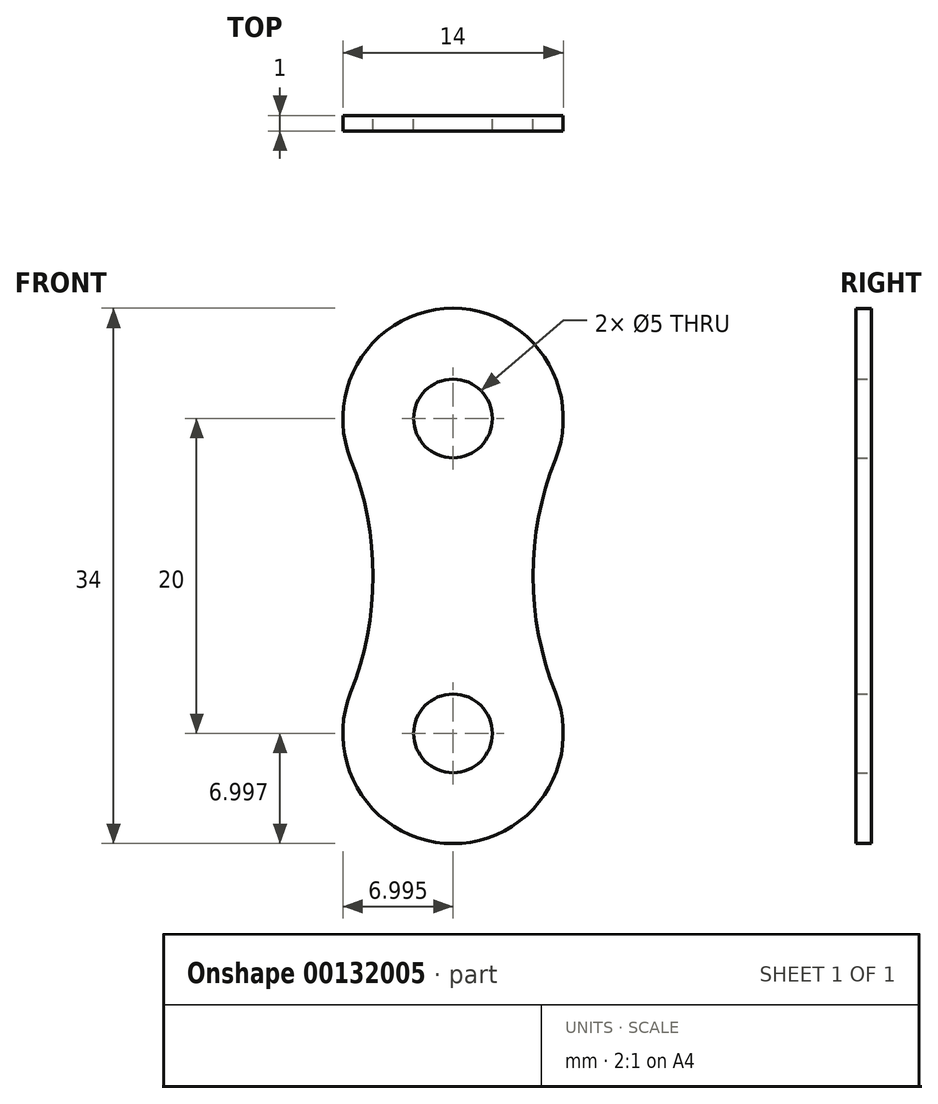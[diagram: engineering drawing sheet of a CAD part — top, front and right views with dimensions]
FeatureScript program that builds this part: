
annotation { "Feature Type Name" : "Feature", "Feature Type Description" : "" }
export const myFeature = defineFeature(function(context is Context, id is Id, definition is map)
    precondition{}
    {
        {
            var Q0;
            Q0=qCreatedBy(makeId("Front.planeOp"),FACE);
            var sketch = newSketch(context, id + "F0", { "sketchPlane" : qUnion([Q0])});
            skArc(sketch, "E0", {"start": v(-39.1, 65.62) * mm, "mid": v(-45.6, 75.22) * mm, "end": v(-52.1, 65.62) * mm});
            skArc(sketch, "E1", {"start": v(-52.1, 50.8) * mm, "mid": v(-45.6, 41.22) * mm, "end": v(-39.1, 50.8) * mm});
            skArc(sketch, "E2", {"start": v(-52.1, 50.8) * mm, "mid": v(-50.68, 58.22) * mm, "end": v(-52.1, 65.62) * mm});
            skArc(sketch, "E3", {"start": v(-39.1, 65.62) * mm, "mid": v(-40.52, 58.22) * mm, "end": v(-39.1, 50.8) * mm});
            skCircle(sketch, "E4", {"center": v(-45.6, 68.22) * mm, "radius": 2.5 * mm});
            skCircle(sketch, "E5", {"center": v(-45.6, 48.22) * mm, "radius": 2.5 * mm});
            skSolve(sketch);
        }
        {
            var Q0;
            Q0=makeQuery(id+"F0.imprint","IMPRINT",FACE,{"disambiguationData":[TD([[makeQuery(id+"F0.imprint","IMPRINT",EDGE,{"derivedFrom":sQuery(id+"F0.wireOp",EDGE,"E0")}),1.0]])]});
            extrude(context, id + "F1", {"entities" : qUnion([Q0]), "depth" : 1 * mm});
        }
    });
